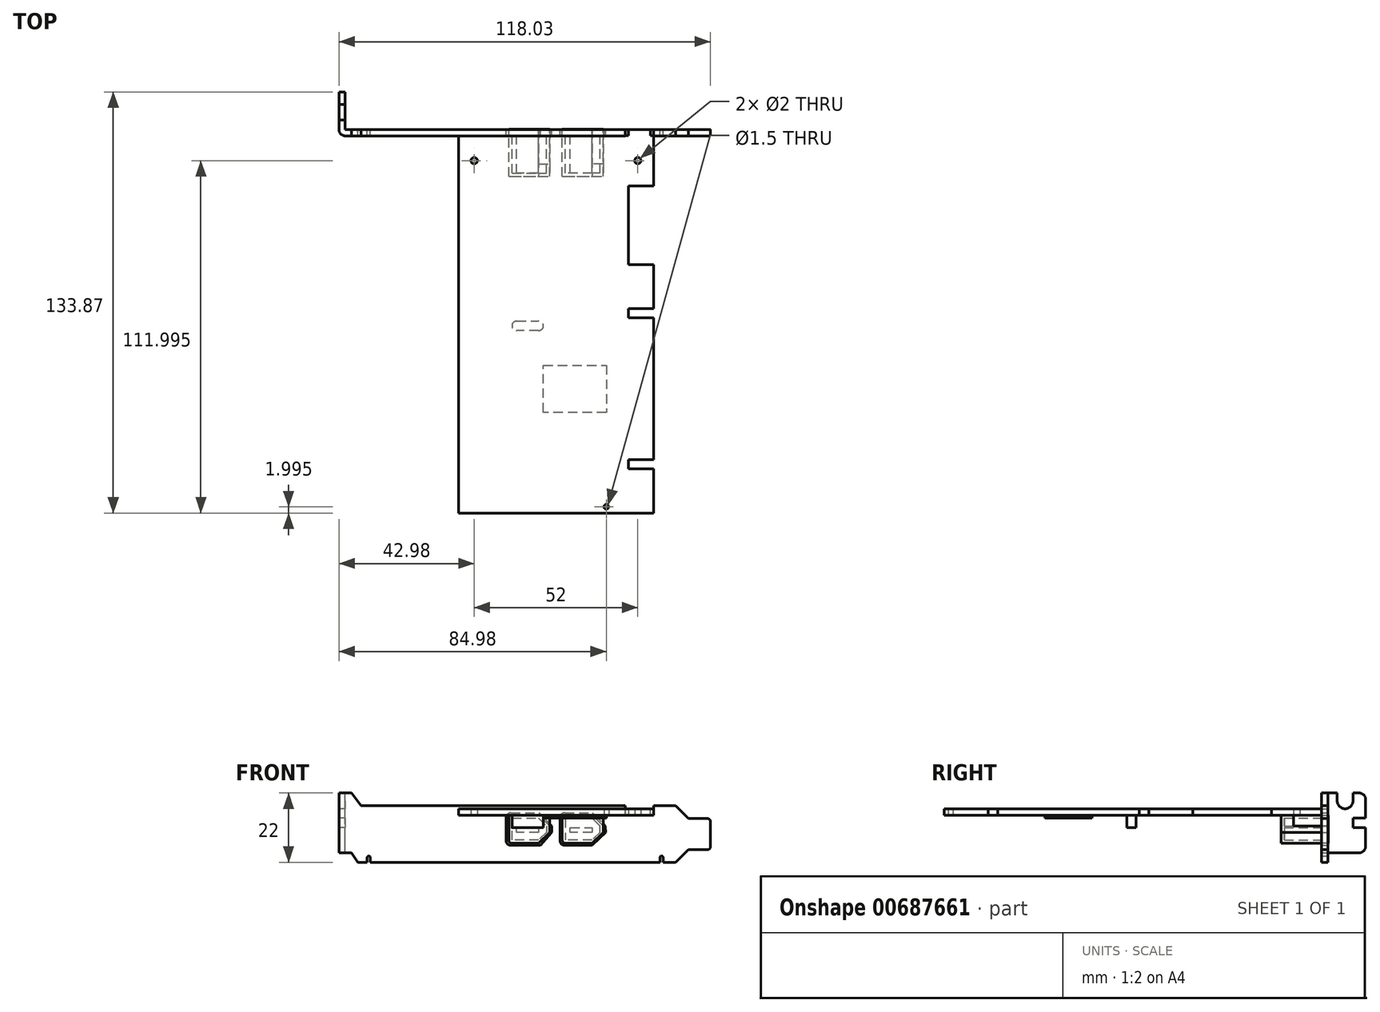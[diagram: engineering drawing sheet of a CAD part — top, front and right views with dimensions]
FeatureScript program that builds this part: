
annotation { "Feature Type Name" : "Feature", "Feature Type Description" : "" }
export const myFeature = defineFeature(function(context is Context, id is Id, definition is map)
    precondition{}
    {
        {
            var Q0;
            Q0=qCreatedBy(makeId("Top.planeOp"),FACE);
            var sketch = newSketch(context, id + "F0", { "sketchPlane" : qUnion([Q0])});
            skLineSegment(sketch, "E0", {"start": v(-31.18, 74.13) * mm, "end": v(-31.18, -45.87) * mm});
            skLineSegment(sketch, "E1", {"start": v(-31.18, -45.87) * mm, "end": v(30.82, -45.87) * mm});
            skLineSegment(sketch, "E2", {"start": v(30.82, -45.87) * mm, "end": v(30.82, -31.87) * mm});
            skLineSegment(sketch, "E3", {"start": v(30.82, -31.87) * mm, "end": v(22.82, -31.87) * mm});
            skLineSegment(sketch, "E4", {"start": v(22.82, -31.87) * mm, "end": v(22.82, -28.87) * mm});
            skLineSegment(sketch, "E5", {"start": v(22.82, -28.87) * mm, "end": v(30.82, -28.87) * mm});
            skLineSegment(sketch, "E6", {"start": v(30.82, -28.87) * mm, "end": v(30.82, 16.13) * mm});
            skLineSegment(sketch, "E7", {"start": v(30.82, 16.13) * mm, "end": v(22.82, 16.13) * mm});
            skLineSegment(sketch, "E8", {"start": v(22.82, 16.13) * mm, "end": v(22.82, 19.13) * mm});
            skLineSegment(sketch, "E9", {"start": v(22.82, 19.13) * mm, "end": v(30.82, 19.13) * mm});
            skLineSegment(sketch, "E10", {"start": v(30.82, 19.13) * mm, "end": v(30.82, 33.13) * mm});
            skLineSegment(sketch, "E11", {"start": v(30.82, 33.13) * mm, "end": v(22.82, 33.13) * mm});
            skLineSegment(sketch, "E12", {"start": v(22.82, 33.13) * mm, "end": v(22.82, 58.13) * mm});
            skLineSegment(sketch, "E13", {"start": v(22.82, 58.13) * mm, "end": v(30.82, 58.13) * mm});
            skLineSegment(sketch, "E14", {"start": v(30.82, 58.13) * mm, "end": v(30.82, 74.13) * mm});
            skLineSegment(sketch, "E15", {"start": v(30.82, 74.13) * mm, "end": v(-31.18, 74.13) * mm});
            skLineSegment(sketch, "E16", {"start": v(22.82, 74.13) * mm, "end": v(22.82, -45.87) * mm});
            skSolve(sketch);
        }
        {
            var Q0;
            Q0 = qSketchRegion(id + "F0", true);
            extrude(context, id + "F1", {"entities" : qUnion([Q0]), "depth" : 2 * mm, "offsetDistance" : 25 * mm});
        }
        {
            var Q0;
            Q0=makeQuery(id+"F1.opExtrude","CAP_FACE",FACE,{"disambiguationData":[OSD([sQuery(id+"F0.wireOp",EDGE,"E0"),sQuery(id+"F0.wireOp",EDGE,"E1"),sQuery(id+"F0.wireOp",EDGE,"E2"),sQuery(id+"F0.wireOp",EDGE,"E3"),sQuery(id+"F0.wireOp",EDGE,"E5"),sQuery(id+"F0.wireOp",EDGE,"E6"),sQuery(id+"F0.wireOp",EDGE,"E7"),sQuery(id+"F0.wireOp",EDGE,"E9"),sQuery(id+"F0.wireOp",EDGE,"E10"),sQuery(id+"F0.wireOp",EDGE,"E11"),sQuery(id+"F0.wireOp",EDGE,"E13"),sQuery(id+"F0.wireOp",EDGE,"E14"),sQuery(id+"F0.wireOp",EDGE,"E15"),sQuery(id+"F0.wireOp",EDGE,"E16")])],"isStart":false});
            var sketch = newSketch(context, id + "F2", { "sketchPlane" : qUnion([Q0])});
            skLineSegment(sketch, "E17", {"start": v(15.82, -17.22) * mm, "end": v(15.82, -13.87) * mm});
            skLineSegment(sketch, "E18", {"start": v(15.82, -13.87) * mm, "end": v(-4.18, -13.87) * mm});
            skLineSegment(sketch, "E19", {"start": v(-4.18, -13.87) * mm, "end": v(-4.18, 1.13) * mm});
            skLineSegment(sketch, "E20", {"start": v(-4.18, 1.13) * mm, "end": v(15.82, 1.13) * mm});
            skLineSegment(sketch, "E21", {"start": v(15.82, 1.13) * mm, "end": v(15.82, -13.87) * mm});
            skPoint(sketch, "E22.end.orphan", {"position": v(15.82, -17.22) * mm});
            skPoint(sketch, "E23.orphan", {"position": v(15.82, -45.87) * mm});
            skSolve(sketch);
        }
        {
            var Q0;
            Q0 = qSketchRegion(id + "F2", true);
            extrude(context, id + "F3", {"entities" : qUnion([Q0]), "operationType" : NewBodyOperationType.ADD, "oppositeDirection" : true, "depth" : 3 * mm, "offsetDistance" : 25 * mm});
        }
        {
            var Q0;
            Q0=makeQuery(id+"F1.opExtrude","CAP_FACE",FACE,{"disambiguationData":[OSD([sQuery(id+"F0.wireOp",EDGE,"E0"),sQuery(id+"F0.wireOp",EDGE,"E1"),sQuery(id+"F0.wireOp",EDGE,"E2"),sQuery(id+"F0.wireOp",EDGE,"E3"),sQuery(id+"F0.wireOp",EDGE,"E5"),sQuery(id+"F0.wireOp",EDGE,"E6"),sQuery(id+"F0.wireOp",EDGE,"E7"),sQuery(id+"F0.wireOp",EDGE,"E9"),sQuery(id+"F0.wireOp",EDGE,"E10"),sQuery(id+"F0.wireOp",EDGE,"E11"),sQuery(id+"F0.wireOp",EDGE,"E13"),sQuery(id+"F0.wireOp",EDGE,"E14"),sQuery(id+"F0.wireOp",EDGE,"E15"),sQuery(id+"F0.wireOp",EDGE,"E16")])],"isStart":true});
            var sketch = newSketch(context, id + "F4", { "sketchPlane" : qUnion([Q0])});
            skLineSegment(sketch, "E24", {"start": v(-5.68, -12.13) * mm, "end": v(-12.68, -12.13) * mm});
            skLineSegment(sketch, "E25", {"start": v(-14.18, -13.63) * mm, "end": v(-14.18, -13.63) * mm});
            skLineSegment(sketch, "E26", {"start": v(-12.68, -15.13) * mm, "end": v(-5.68, -15.13) * mm});
            skLineSegment(sketch, "E27", {"start": v(-5.68, -15.13) * mm, "end": v(-12.68, -15.13) * mm});
            skLineSegment(sketch, "E28", {"start": v(-4.18, -13.63) * mm, "end": v(-4.18, -13.63) * mm});
            skPoint(sketch, "E29.visualSharp", {"position": v(-14.18, -12.13) * mm});
            skArc(sketch, "E29.filletArc", {"start": v(-12.68, -12.13) * mm, "mid": v(-13.74, -12.56) * mm, "end": v(-14.18, -13.63) * mm});
            skPoint(sketch, "E30.visualSharp", {"position": v(-14.18, -15.13) * mm});
            skArc(sketch, "E30.filletArc", {"start": v(-14.18, -13.63) * mm, "mid": v(-13.74, -14.69) * mm, "end": v(-12.68, -15.13) * mm});
            skPoint(sketch, "E31.visualSharp", {"position": v(-4.18, -12.13) * mm});
            skArc(sketch, "E31.filletArc", {"start": v(-4.18, -13.63) * mm, "mid": v(-4.62, -12.56) * mm, "end": v(-5.68, -12.13) * mm});
            skPoint(sketch, "E32.visualSharp", {"position": v(-4.18, -15.13) * mm});
            skArc(sketch, "E32.filletArc", {"start": v(-5.68, -15.13) * mm, "mid": v(-4.62, -14.69) * mm, "end": v(-4.18, -13.63) * mm});
            skPoint(sketch, "E33.start.orphan", {"position": v(-14.18, -13.63) * mm});
            skSolve(sketch);
        }
        {
            var Q0;
            Q0 = qSketchRegion(id + "F4", true);
            extrude(context, id + "F5", {"entities" : qUnion([Q0]), "operationType" : NewBodyOperationType.ADD, "depth" : 4 * mm, "offsetDistance" : 25 * mm});
        }
        {
            var Q0;
            Q0=makeQuery(id+"F1.opExtrude","CAP_FACE",FACE,{"disambiguationData":[OSD([sQuery(id+"F0.wireOp",EDGE,"E0"),sQuery(id+"F0.wireOp",EDGE,"E1"),sQuery(id+"F0.wireOp",EDGE,"E2"),sQuery(id+"F0.wireOp",EDGE,"E3"),sQuery(id+"F0.wireOp",EDGE,"E5"),sQuery(id+"F0.wireOp",EDGE,"E6"),sQuery(id+"F0.wireOp",EDGE,"E7"),sQuery(id+"F0.wireOp",EDGE,"E9"),sQuery(id+"F0.wireOp",EDGE,"E10"),sQuery(id+"F0.wireOp",EDGE,"E11"),sQuery(id+"F0.wireOp",EDGE,"E13"),sQuery(id+"F0.wireOp",EDGE,"E14"),sQuery(id+"F0.wireOp",EDGE,"E15"),sQuery(id+"F0.wireOp",EDGE,"E16")])],"isStart":true});
            var sketch = newSketch(context, id + "F6", { "sketchPlane" : qUnion([Q0])});
            skLineSegment(sketch, "E34", {"start": v(22.82, 45.87) * mm, "end": v(22.82, -74.13) * mm});
            skPoint(sketch, "E35.end.orphan", {"position": v(15.82, 43.43) * mm});
            skCircle(sketch, "E36", {"center": v(15.82, 43.87) * mm, "radius": 0.75 * mm});
            skPoint(sketch, "E37.orphan", {"position": v(15.82, 45.87) * mm});
            skSolve(sketch);
        }
        {
            var Q0;
            Q0 = qSketchRegion(id + "F6", true);
            extrude(context, id + "F7", {"entities" : qUnion([Q0]), "operationType" : NewBodyOperationType.REMOVE, "oppositeDirection" : true, "depth" : 25 * mm, "offsetDistance" : 25 * mm});
        }
        {
            var Q0;
            Q0=makeQuery(id+"F1.opExtrude","CAP_FACE",FACE,{"disambiguationData":[OSD([sQuery(id+"F0.wireOp",EDGE,"E0"),sQuery(id+"F0.wireOp",EDGE,"E1"),sQuery(id+"F0.wireOp",EDGE,"E2"),sQuery(id+"F0.wireOp",EDGE,"E3"),sQuery(id+"F0.wireOp",EDGE,"E5"),sQuery(id+"F0.wireOp",EDGE,"E6"),sQuery(id+"F0.wireOp",EDGE,"E7"),sQuery(id+"F0.wireOp",EDGE,"E9"),sQuery(id+"F0.wireOp",EDGE,"E10"),sQuery(id+"F0.wireOp",EDGE,"E11"),sQuery(id+"F0.wireOp",EDGE,"E13"),sQuery(id+"F0.wireOp",EDGE,"E14"),sQuery(id+"F0.wireOp",EDGE,"E15"),sQuery(id+"F0.wireOp",EDGE,"E16")])],"isStart":true});
            var sketch = newSketch(context, id + "F8", { "sketchPlane" : qUnion([Q0])});
            skCircle(sketch, "E38", {"center": v(25.82, -66.13) * mm, "radius": 1 * mm});
            skPoint(sketch, "E39.orphan", {"position": v(30.82, -66.13) * mm});
            skCircle(sketch, "E40", {"center": v(-26.18, -66.13) * mm, "radius": 1 * mm});
            skPoint(sketch, "E41.orphan", {"position": v(-31.18, -66.13) * mm});
            skSolve(sketch);
        }
        {
            var Q0;
            Q0 = qSketchRegion(id + "F8", true);
            extrude(context, id + "F9", {"entities" : qUnion([Q0]), "operationType" : NewBodyOperationType.REMOVE, "oppositeDirection" : true, "depth" : 25 * mm, "offsetDistance" : 25 * mm});
        }
        {
            var Q0;
            Q0=makeQuery(id+"F1.opExtrude","CAP_FACE",FACE,{"disambiguationData":[OSD([sQuery(id+"F0.wireOp",EDGE,"E0"),sQuery(id+"F0.wireOp",EDGE,"E1"),sQuery(id+"F0.wireOp",EDGE,"E2"),sQuery(id+"F0.wireOp",EDGE,"E3"),sQuery(id+"F0.wireOp",EDGE,"E5"),sQuery(id+"F0.wireOp",EDGE,"E6"),sQuery(id+"F0.wireOp",EDGE,"E7"),sQuery(id+"F0.wireOp",EDGE,"E9"),sQuery(id+"F0.wireOp",EDGE,"E10"),sQuery(id+"F0.wireOp",EDGE,"E11"),sQuery(id+"F0.wireOp",EDGE,"E13"),sQuery(id+"F0.wireOp",EDGE,"E14"),sQuery(id+"F0.wireOp",EDGE,"E15"),sQuery(id+"F0.wireOp",EDGE,"E16")])],"isStart":true});
            var sketch = newSketch(context, id + "F10", { "sketchPlane" : qUnion([Q0])});
            skLineSegment(sketch, "E42", {"start": v(14.82, -74.13) * mm, "end": v(14.82, -61.13) * mm});
            skLineSegment(sketch, "E43", {"start": v(1.82, -61.13) * mm, "end": v(1.82, -74.13) * mm});
            skLineSegment(sketch, "E44", {"start": v(-15.18, -74.13) * mm, "end": v(-15.18, -61.13) * mm});
            skLineSegment(sketch, "E45", {"start": v(-2.18, -61.13) * mm, "end": v(-2.18, -74.13) * mm});
            skPoint(sketch, "E46.end.orphan", {"position": v(14.82, -67.43) * mm});
            skPoint(sketch, "E47.end.orphan", {"position": v(-15.18, -67.9) * mm});
            skPoint(sketch, "E47.start.orphan", {"position": v(-31.18, -67.43) * mm});
            skLineSegment(sketch, "E48", {"start": v(-15.18, -61.13) * mm, "end": v(-2.18, -61.13) * mm});
            skLineSegment(sketch, "E49", {"start": v(1.82, -61.13) * mm, "end": v(14.82, -61.13) * mm});
            skLineSegment(sketch, "E50", {"start": v(-15.18, -74.13) * mm, "end": v(-15.18, -76.13) * mm});
            skLineSegment(sketch, "E51", {"start": v(-2.18, -76.13) * mm, "end": v(-2.18, -74.13) * mm});
            skLineSegment(sketch, "E52", {"start": v(1.82, -74.13) * mm, "end": v(1.82, -76.13) * mm});
            skLineSegment(sketch, "E53", {"start": v(14.82, -76.13) * mm, "end": v(14.82, -74.13) * mm});
            skLineSegment(sketch, "E54", {"start": v(-15.18, -76.13) * mm, "end": v(-2.18, -76.13) * mm});
            skLineSegment(sketch, "E55", {"start": v(1.82, -76.13) * mm, "end": v(14.82, -76.13) * mm});
            skSolve(sketch);
        }
        {
            var Q0;
            Q0 = qSketchRegion(id + "F10", true);
            extrude(context, id + "F11", {"entities" : qUnion([Q0]), "operationType" : NewBodyOperationType.ADD, "depth" : 9 * mm, "offsetDistance" : 25 * mm});
        }
        {
            var Q0;
            Q0=makeQuery(id+"F11.opExtrude","CAP_EDGE",EDGE,{"disambiguationData":[OSD([sQuery(id+"F10.wireOp",EDGE,"E42"),sQuery(id+"F10.wireOp",EDGE,"E53")])],"isStart":false});
            chamfer(context, id + "F12", {"entities" : qUnion([Q0]), "width" : 3.5 * mm, "tangentPropagation" : true});
        }
        {
            var Q0;
            {var subQ0=sQuery(id+"F10.wireOp",EDGE,"E53");var subQ1=sQuery(id+"F10.wireOp",EDGE,"E42");Q0=makeQuery(id+"F11.boolean.opBoolean","SPLIT",EDGE,{"disambiguationData":[topologyDisambiguationEdgeConnected([makeQuery(id+"F11.opExtrude","CAP_FACE",FACE,{"disambiguationData":[OSD([subQ1,sQuery(id+"F10.wireOp",EDGE,"E43"),sQuery(id+"F10.wireOp",EDGE,"E49"),sQuery(id+"F10.wireOp",EDGE,"E52"),subQ0,sQuery(id+"F10.wireOp",EDGE,"E55")])],"isStart":true})])],"derivedFrom":makeQuery(id+"F11.opExtrude","CAP_EDGE",EDGE,{"disambiguationData":[OSD([subQ1,subQ0])],"isStart":true})});}
            chamfer(context, id + "F13", {"entities" : qUnion([Q0]), "width" : 3.5 * mm, "tangentPropagation" : true});
        }
        {
            var Q0;
            Q0=makeQuery(id+"F11.opExtrude","CAP_EDGE",EDGE,{"disambiguationData":[OSD([sQuery(id+"F10.wireOp",EDGE,"E43"),sQuery(id+"F10.wireOp",EDGE,"E52")])],"isStart":false});
            fillet(context, id + "F14", {"entities" : qUnion([Q0]), "radius" : 1 * mm, "tangentPropagation" : true, "allowEdgeOverflow" : false});
        }
        {
            var Q0;
            Q0=makeQuery(id+"F11.opExtrude","CAP_EDGE",EDGE,{"disambiguationData":[OSD([sQuery(id+"F10.wireOp",EDGE,"E44"),sQuery(id+"F10.wireOp",EDGE,"E50")])],"isStart":false});
            fillet(context, id + "F15", {"entities" : qUnion([Q0]), "radius" : 1 * mm, "tangentPropagation" : true, "allowEdgeOverflow" : false});
        }
        {
            var Q0;
            Q0=makeQuery(id+"F11.opExtrude","CAP_EDGE",EDGE,{"disambiguationData":[OSD([sQuery(id+"F10.wireOp",EDGE,"E45"),sQuery(id+"F10.wireOp",EDGE,"E51")])],"isStart":false});
            var Q1;
            {var subQ0=sQuery(id+"F10.wireOp",EDGE,"E51");var subQ1=sQuery(id+"F10.wireOp",EDGE,"E45");Q1=makeQuery(id+"F11.boolean.opBoolean","SPLIT",EDGE,{"disambiguationData":[topologyDisambiguationEdgeConnected([makeQuery(id+"F11.opExtrude","CAP_FACE",FACE,{"disambiguationData":[OSD([sQuery(id+"F10.wireOp",EDGE,"E44"),subQ1,sQuery(id+"F10.wireOp",EDGE,"E48"),sQuery(id+"F10.wireOp",EDGE,"E50"),subQ0,sQuery(id+"F10.wireOp",EDGE,"E54")])],"isStart":true})])],"derivedFrom":makeQuery(id+"F11.opExtrude","CAP_EDGE",EDGE,{"disambiguationData":[OSD([subQ1,subQ0])],"isStart":true})});}
            chamfer(context, id + "F16", {"entities" : qUnion([Q0, Q1]), "width" : 3.5 * mm, "tangentPropagation" : true});
        }
        {
            var Q0;
            Q0=makeQuery(id+"F11.opExtrude","SWEPT_FACE",FACE,{"disambiguationData":[OSD([sQuery(id+"F10.wireOp",EDGE,"E54")])]});
            var sketch = newSketch(context, id + "F17", { "sketchPlane" : qUnion([Q0])});
            skLineSegment(sketch, "E56", {"start": v(14.18, -1) * mm, "end": v(5.68, -1) * mm});
            skLineSegment(sketch, "E57", {"start": v(5.68, -1) * mm, "end": v(3.18, -3.5) * mm});
            skLineSegment(sketch, "E58", {"start": v(3.18, -3.5) * mm, "end": v(3.18, -5.5) * mm});
            skLineSegment(sketch, "E59", {"start": v(3.18, -5.5) * mm, "end": v(5.68, -8) * mm});
            skLineSegment(sketch, "E60", {"start": v(5.68, -8) * mm, "end": v(14.18, -8) * mm});
            skPoint(sketch, "E61.start.orphan", {"position": v(15.18, -4) * mm});
            skPoint(sketch, "E62.end.orphan", {"position": v(10.43, -1) * mm});
            skPoint(sketch, "E62.start.orphan", {"position": v(10.43, 0) * mm});
            skPoint(sketch, "E63.orphan", {"position": v(3.93, -1.75) * mm});
            skPoint(sketch, "E64.end.orphan", {"position": v(3.18, -4.5) * mm});
            skPoint(sketch, "E64.start.orphan", {"position": v(2.18, -4.5) * mm});
            skPoint(sketch, "E65.orphan", {"position": v(3.93, -7.25) * mm});
            skPoint(sketch, "E66.end.orphan", {"position": v(4.64, -6.54) * mm});
            skPoint(sketch, "E67.end.orphan", {"position": v(4.64, -2.46) * mm});
            skPoint(sketch, "E68.end.orphan", {"position": v(9.93, -8) * mm});
            skPoint(sketch, "E68.start.orphan", {"position": v(9.93, -9) * mm});
            skLineSegment(sketch, "E69", {"start": v(14.18, -8) * mm, "end": v(14.18, -1) * mm});
            skLineSegment(sketch, "E70", {"start": v(5.68, -5.5) * mm, "end": v(12.68, -5.5) * mm});
            skLineSegment(sketch, "E71", {"start": v(12.68, -5.5) * mm, "end": v(12.68, -4) * mm});
            skLineSegment(sketch, "E72", {"start": v(12.68, -4) * mm, "end": v(5.68, -4) * mm});
            skLineSegment(sketch, "E73", {"start": v(5.68, -4) * mm, "end": v(5.68, -5.5) * mm});
            skSolve(sketch);
        }
        {
            var Q0;
            Q0=makeQuery(id+"F17.imprint","IMPRINT",FACE,{"disambiguationData":[TD([[makeQuery(id+"F17.imprint","IMPRINT",EDGE,{"derivedFrom":sQuery(id+"F17.wireOp",EDGE,"E56")}),1.0]])]});
            extrude(context, id + "F18", {"entities" : qUnion([Q0]), "operationType" : NewBodyOperationType.REMOVE, "oppositeDirection" : true, "depth" : 14 * mm, "offsetDistance" : 25 * mm});
        }
        {
            var Q0;
            Q0=makeQuery(id+"F18.boolean.opBoolean","SPLIT",FACE,{"disambiguationData":[TD([makeQuery(id+"F18.opExtrude","SWEPT_FACE",FACE,{"disambiguationData":[OSD([sQuery(id+"F17.wireOp",EDGE,"E70")])]})])],"derivedFrom":makeQuery(id+"F11.opExtrude","SWEPT_FACE",FACE,{"disambiguationData":[OSD([sQuery(id+"F10.wireOp",EDGE,"E54")])]})});
            extrude(context, id + "F19", {"entities" : qUnion([Q0]), "operationType" : NewBodyOperationType.REMOVE, "oppositeDirection" : true, "depth" : 2 * mm, "offsetDistance" : 25 * mm});
        }
        {
            var Q0;
            Q0=makeQuery(id+"F11.opExtrude","SWEPT_FACE",FACE,{"disambiguationData":[OSD([sQuery(id+"F10.wireOp",EDGE,"E55")])]});
            var sketch = newSketch(context, id + "F20", { "sketchPlane" : qUnion([Q0])});
            skLineSegment(sketch, "E74", {"start": v(-2.82, -4) * mm, "end": v(-2.82, -8) * mm});
            skLineSegment(sketch, "E75", {"start": v(-2.82, -8) * mm, "end": v(-2.82, -1) * mm});
            skLineSegment(sketch, "E76", {"start": v(-2.82, -1) * mm, "end": v(-11.32, -1) * mm});
            skLineSegment(sketch, "E77", {"start": v(-13.82, -3.5) * mm, "end": v(-11.32, -1) * mm});
            skLineSegment(sketch, "E78", {"start": v(-13.82, -5.5) * mm, "end": v(-11.32, -8) * mm});
            skLineSegment(sketch, "E79", {"start": v(-11.32, -8) * mm, "end": v(-2.82, -8) * mm});
            skLineSegment(sketch, "E80", {"start": v(-13.82, -5.5) * mm, "end": v(-13.82, -3.5) * mm});
            skPoint(sketch, "E81.end.orphan", {"position": v(-7.07, -8) * mm});
            skPoint(sketch, "E81.start.orphan", {"position": v(-7.07, -9) * mm});
            skPoint(sketch, "E82.start.orphan", {"position": v(-1.82, -4) * mm});
            skPoint(sketch, "E83.end.orphan", {"position": v(-7.07, -1) * mm});
            skPoint(sketch, "E83.start.orphan", {"position": v(-7.07, 0) * mm});
            skLineSegment(sketch, "E84", {"start": v(-11.32, -5.5) * mm, "end": v(-4.32, -5.5) * mm});
            skLineSegment(sketch, "E85", {"start": v(-4.32, -5.5) * mm, "end": v(-4.32, -4) * mm});
            skLineSegment(sketch, "E86", {"start": v(-4.32, -4) * mm, "end": v(-11.32, -4) * mm});
            skLineSegment(sketch, "E87", {"start": v(-11.32, -4) * mm, "end": v(-11.32, -5.5) * mm});
            skSolve(sketch);
        }
        {
            var Q0;
            {var subQ3=sQuery(id+"F20.wireOp",EDGE,"E76");Q0=makeQuery(id+"F20.imprint","IMPRINT",FACE,{"disambiguationData":[TD([[makeQuery(id+"F20.imprint","IMPRINT",EDGE,{"derivedFrom":subQ3}),1.0]])]});}
            extrude(context, id + "F21", {"entities" : qUnion([Q0]), "operationType" : NewBodyOperationType.REMOVE, "oppositeDirection" : true, "depth" : 14 * mm, "offsetDistance" : 25 * mm});
        }
        {
            var Q0;
            Q0=makeQuery(id+"F21.boolean.opBoolean","SPLIT",FACE,{"disambiguationData":[TD([makeQuery(id+"F21.opExtrude","SWEPT_FACE",FACE,{"disambiguationData":[OSD([sQuery(id+"F20.wireOp",EDGE,"E84")])]})])],"derivedFrom":makeQuery(id+"F11.opExtrude","SWEPT_FACE",FACE,{"disambiguationData":[OSD([sQuery(id+"F10.wireOp",EDGE,"E55")])]})});
            extrude(context, id + "F22", {"entities" : qUnion([Q0]), "operationType" : NewBodyOperationType.REMOVE, "oppositeDirection" : true, "depth" : 2 * mm, "offsetDistance" : 25 * mm});
        }
        {
            var Q0;
            Q0=makeQuery(id+"F1.opExtrude","SWEPT_FACE",FACE,{"disambiguationData":[OSD([sQuery(id+"F0.wireOp",EDGE,"E15")])]});
            var sketch = newSketch(context, id + "F23", { "sketchPlane" : qUnion([Q0])});
            skLineSegment(sketch, "E88", {"start": v(-14.82, 0) * mm, "end": v(-11.32, 0) * mm});
            skLineSegment(sketch, "E89", {"start": v(-11.32, 0) * mm, "end": v(-14.82, -3.5) * mm});
            skLineSegment(sketch, "E90", {"start": v(-14.82, -3.5) * mm, "end": v(-14.82, 0) * mm});
            skLineSegment(sketch, "E91", {"start": v(2.18, 0) * mm, "end": v(2.18, -3.5) * mm});
            skLineSegment(sketch, "E92", {"start": v(2.18, -3.5) * mm, "end": v(5.68, 0) * mm});
            skLineSegment(sketch, "E93", {"start": v(5.68, 0) * mm, "end": v(2.18, 0) * mm});
            skSolve(sketch);
        }
        {
            var Q0;
            Q0=makeQuery(id+"F23.imprint","IMPRINT",FACE,{"disambiguationData":[TD([[makeQuery(id+"F23.imprint","IMPRINT",EDGE,{"derivedFrom":sQuery(id+"F23.wireOp",EDGE,"E88")}),-1.0]])]});
            extrude(context, id + "F24", {"entities" : qUnion([Q0]), "operationType" : NewBodyOperationType.REMOVE, "oppositeDirection" : true, "depth" : 9 * mm, "offsetDistance" : 25 * mm});
        }
        {
            var Q0;
            Q0=makeQuery(id+"F1.opExtrude","SWEPT_FACE",FACE,{"disambiguationData":[OSD([sQuery(id+"F0.wireOp",EDGE,"E15")])]});
            var sketch = newSketch(context, id + "F25", { "sketchPlane" : qUnion([Q0])});
            skLineSegment(sketch, "E94", {"start": v(5.68, 0) * mm, "end": v(2.18, 0) * mm});
            skLineSegment(sketch, "E95", {"start": v(2.18, 0) * mm, "end": v(2.18, -3.5) * mm});
            skLineSegment(sketch, "E96", {"start": v(2.18, -3.5) * mm, "end": v(5.68, 0) * mm});
            skSolve(sketch);
        }
        {
            var Q0;
            Q0=makeQuery(id+"F25.imprint","IMPRINT",FACE,{"disambiguationData":[TD([[makeQuery(id+"F25.imprint","IMPRINT",EDGE,{"derivedFrom":sQuery(id+"F25.wireOp",EDGE,"E94")}),1.0]])]});
            extrude(context, id + "F26", {"entities" : qUnion([Q0]), "operationType" : NewBodyOperationType.REMOVE, "oppositeDirection" : true, "depth" : 9 * mm, "offsetDistance" : 25 * mm});
        }
        {
            var Q0;
            Q0=qCreatedBy(makeId("Front.planeOp"),FACE);
            cPlane(context, id + "F27", {"entities" : qUnion([Q0]), "cplaneType" : CPlaneType.OFFSET, "offset" : 76 * mm, "oppositeDirection" : true, "width" : 150 * mm, "height" : 150 * mm});
        }
        {
            var Q0;
            Q0=qCreatedBy(id+"F27.planeOp",FACE);
            var sketch = newSketch(context, id + "F28", { "sketchPlane" : qUnion([Q0])});
            skLineSegment(sketch, "E97", {"start": v(1.84, 3) * mm, "end": v(21.84, 3) * mm});
            skLineSegment(sketch, "E98", {"start": v(21.84, 3) * mm, "end": v(21.84, 0.5) * mm});
            skLineSegment(sketch, "E99", {"start": v(22.34, 0) * mm, "end": v(22.34, 0) * mm});
            skLineSegment(sketch, "E100", {"start": v(22.84, 0.5) * mm, "end": v(22.84, 2) * mm});
            skLineSegment(sketch, "E101", {"start": v(22.84, 2) * mm, "end": v(29.84, 2) * mm});
            skLineSegment(sketch, "E102", {"start": v(29.84, 2) * mm, "end": v(29.84, 0.5) * mm});
            skLineSegment(sketch, "E103", {"start": v(30.34, 0) * mm, "end": v(30.34, 0) * mm});
            skLineSegment(sketch, "E104", {"start": v(30.84, 0.5) * mm, "end": v(30.84, 3) * mm});
            skLineSegment(sketch, "E105", {"start": v(30.84, 3) * mm, "end": v(37.84, 3) * mm});
            skLineSegment(sketch, "E106", {"start": v(48.87, -6.04) * mm, "end": v(48.87, -2.04) * mm});
            skLineSegment(sketch, "E107", {"start": v(37.84, -15) * mm, "end": v(33.84, -15) * mm});
            skLineSegment(sketch, "E108", {"start": v(33.84, -15) * mm, "end": v(33.84, -13.5) * mm});
            skLineSegment(sketch, "E109", {"start": v(33.34, -13) * mm, "end": v(33.34, -13) * mm});
            skLineSegment(sketch, "E110", {"start": v(32.84, -13.5) * mm, "end": v(32.84, -15) * mm});
            skLineSegment(sketch, "E111", {"start": v(32.84, -15) * mm, "end": v(-59.16, -15) * mm});
            skLineSegment(sketch, "E112", {"start": v(-59.16, -15) * mm, "end": v(-59.16, -13.5) * mm});
            skLineSegment(sketch, "E113", {"start": v(-59.66, -13) * mm, "end": v(-59.66, -13) * mm});
            skLineSegment(sketch, "E114", {"start": v(-60.16, -13.5) * mm, "end": v(-60.16, -15) * mm});
            skLineSegment(sketch, "E115", {"start": v(-60.16, -15) * mm, "end": v(-63.16, -15) * mm});
            skLineSegment(sketch, "E116", {"start": v(-63.16, -15) * mm, "end": v(-65.16, -12) * mm});
            skLineSegment(sketch, "E117", {"start": v(0, 3) * mm, "end": v(-62.16, 3) * mm});
            skLineSegment(sketch, "E118", {"start": v(-62.16, 3) * mm, "end": v(-65.16, 7) * mm});
            skPoint(sketch, "E119.start.orphan", {"position": v(-62.16, 4) * mm});
            skLineSegment(sketch, "E120", {"start": v(-9.45, 0) * mm, "end": v(-9.45, 0.7) * mm});
            skLineSegment(sketch, "E121", {"start": v(-15.34, -4.2) * mm, "end": v(-16.04, -4.2) * mm});
            skLineSegment(sketch, "E122", {"start": v(-9.92, -8.95) * mm, "end": v(-9.92, -9.65) * mm});
            skLineSegment(sketch, "E123", {"start": v(-9.92, -9.65) * mm, "end": v(-14.54, -9.65) * mm});
            skLineSegment(sketch, "E124", {"start": v(-16.04, -8.15) * mm, "end": v(-16.04, -4.2) * mm});
            skLineSegment(sketch, "E125", {"start": v(-16.04, -4.2) * mm, "end": v(-16.04, -0.8) * mm});
            skLineSegment(sketch, "E126", {"start": v(-14.54, 0.7) * mm, "end": v(-9.45, 0.7) * mm});
            skLineSegment(sketch, "E127", {"start": v(-5.6, 0) * mm, "end": v(-5.6, 0.7) * mm});
            skLineSegment(sketch, "E128", {"start": v(-5.6, 0.7) * mm, "end": v(-9.45, 0.7) * mm});
            skLineSegment(sketch, "E129", {"start": v(-2.2, -3.53) * mm, "end": v(-1.5, -3.53) * mm});
            skLineSegment(sketch, "E130", {"start": v(-1.5, -3.53) * mm, "end": v(-5.6, 0.7) * mm});
            skLineSegment(sketch, "E131", {"start": v(-2.2, -5.52) * mm, "end": v(-1.5, -5.52) * mm});
            skLineSegment(sketch, "E132", {"start": v(-1.5, -5.52) * mm, "end": v(-1.5, -3.53) * mm});
            skLineSegment(sketch, "E133", {"start": v(-5.6, -9.12) * mm, "end": v(-5.1, -9.62) * mm});
            skLineSegment(sketch, "E134", {"start": v(-5.1, -9.62) * mm, "end": v(-1.5, -5.52) * mm});
            skLineSegment(sketch, "E135", {"start": v(-9.92, -9.65) * mm, "end": v(-5.1, -9.62) * mm});
            skPoint(sketch, "E136.visualSharp", {"position": v(-16.04, -9.65) * mm});
            skArc(sketch, "E136.filletArc", {"start": v(-16.04, -8.15) * mm, "mid": v(-15.6, -9.2) * mm, "end": v(-14.54, -9.65) * mm});
            skPoint(sketch, "E137.visualSharp", {"position": v(-16.04, 0.7) * mm});
            skArc(sketch, "E137.filletArc", {"start": v(-14.54, 0.7) * mm, "mid": v(-15.6, 0.26) * mm, "end": v(-16.04, -0.8) * mm});
            skLineSegment(sketch, "E138", {"start": v(7.34, 0) * mm, "end": v(7.34, 0.7) * mm});
            skLineSegment(sketch, "E139", {"start": v(14.82, -3.47) * mm, "end": v(15.52, -3.47) * mm});
            skLineSegment(sketch, "E140", {"start": v(14.85, -5.53) * mm, "end": v(15.55, -5.53) * mm});
            skLineSegment(sketch, "E141", {"start": v(11.27, -9.14) * mm, "end": v(11.27, -9.62) * mm});
            skLineSegment(sketch, "E142", {"start": v(11.27, -9.62) * mm, "end": v(15.55, -5.53) * mm});
            skLineSegment(sketch, "E143", {"start": v(15.52, -3.47) * mm, "end": v(15.55, -5.53) * mm});
            skLineSegment(sketch, "E144", {"start": v(11.42, 0) * mm, "end": v(11.42, 0.7) * mm});
            skLineSegment(sketch, "E145", {"start": v(11.42, 0.7) * mm, "end": v(7.34, 0.7) * mm});
            skLineSegment(sketch, "E146", {"start": v(11.42, 0.7) * mm, "end": v(15.52, -3.47) * mm});
            skLineSegment(sketch, "E147", {"start": v(0, 3) * mm, "end": v(1.84, 3) * mm});
            skPoint(sketch, "E148.start.orphan", {"position": v(1.84, 0) * mm});
            skPoint(sketch, "E149.start.orphan", {"position": v(1.33, 0.7) * mm});
            skLineSegment(sketch, "E150", {"start": v(1.8, -4) * mm, "end": v(1.1, -4) * mm});
            skLineSegment(sketch, "E151", {"start": v(11.27, -9.62) * mm, "end": v(2.6, -9.62) * mm});
            skLineSegment(sketch, "E152", {"start": v(1.1, -8.12) * mm, "end": v(1.1, -4) * mm});
            skLineSegment(sketch, "E153", {"start": v(7.34, 0.7) * mm, "end": v(2.6, 0.7) * mm});
            skLineSegment(sketch, "E154", {"start": v(1.1, -0.8) * mm, "end": v(1.1, -4) * mm});
            skPoint(sketch, "E155.visualSharp", {"position": v(1.1, -9.62) * mm});
            skArc(sketch, "E155.filletArc", {"start": v(1.1, -8.12) * mm, "mid": v(1.53, -9.18) * mm, "end": v(2.6, -9.62) * mm});
            skPoint(sketch, "E156.visualSharp", {"position": v(1.1, 0.7) * mm});
            skArc(sketch, "E156.filletArc", {"start": v(2.6, 0.7) * mm, "mid": v(1.53, 0.26) * mm, "end": v(1.1, -0.8) * mm});
            skPoint(sketch, "E157.visualSharp", {"position": v(33.84, -13) * mm});
            skArc(sketch, "E157.filletArc", {"start": v(33.84, -13.5) * mm, "mid": v(33.7, -13.15) * mm, "end": v(33.34, -13) * mm});
            skPoint(sketch, "E158.visualSharp", {"position": v(32.84, -13) * mm});
            skArc(sketch, "E158.filletArc", {"start": v(33.34, -13) * mm, "mid": v(33, -13.15) * mm, "end": v(32.84, -13.5) * mm});
            skPoint(sketch, "E159.visualSharp", {"position": v(30.84, 0) * mm});
            skArc(sketch, "E159.filletArc", {"start": v(30.34, 0) * mm, "mid": v(30.7, 0.15) * mm, "end": v(30.84, 0.5) * mm});
            skPoint(sketch, "E160.visualSharp", {"position": v(29.84, 0) * mm});
            skArc(sketch, "E160.filletArc", {"start": v(29.84, 0.5) * mm, "mid": v(30, 0.15) * mm, "end": v(30.34, 0) * mm});
            skPoint(sketch, "E161.visualSharp", {"position": v(22.84, 0) * mm});
            skArc(sketch, "E161.filletArc", {"start": v(22.34, 0) * mm, "mid": v(22.7, 0.15) * mm, "end": v(22.84, 0.5) * mm});
            skPoint(sketch, "E162.visualSharp", {"position": v(21.84, 0) * mm});
            skArc(sketch, "E162.filletArc", {"start": v(21.84, 0.5) * mm, "mid": v(22, 0.15) * mm, "end": v(22.34, 0) * mm});
            skPoint(sketch, "E163.visualSharp", {"position": v(-59.16, -13) * mm});
            skArc(sketch, "E163.filletArc", {"start": v(-59.16, -13.5) * mm, "mid": v(-59.3, -13.15) * mm, "end": v(-59.66, -13) * mm});
            skPoint(sketch, "E164.visualSharp", {"position": v(-60.16, -13) * mm});
            skArc(sketch, "E164.filletArc", {"start": v(-59.66, -13) * mm, "mid": v(-60, -13.15) * mm, "end": v(-60.16, -13.5) * mm});
            skPoint(sketch, "E165.start.orphan", {"position": v(37.84, -6) * mm});
            skLineSegment(sketch, "E166", {"start": v(48.87, -6.04) * mm, "end": v(48.87, -10.04) * mm});
            skLineSegment(sketch, "E167", {"start": v(47.87, -11.04) * mm, "end": v(41.87, -11.04) * mm});
            skLineSegment(sketch, "E168", {"start": v(41.87, -11.04) * mm, "end": v(37.84, -15) * mm});
            skLineSegment(sketch, "E169", {"start": v(47.87, -1.04) * mm, "end": v(41.87, -1.04) * mm});
            skLineSegment(sketch, "E170", {"start": v(41.87, -1.04) * mm, "end": v(37.84, 3) * mm});
            skPoint(sketch, "E171.visualSharp", {"position": v(48.87, -11.04) * mm});
            skArc(sketch, "E171.filletArc", {"start": v(47.87, -11.04) * mm, "mid": v(48.57, -10.75) * mm, "end": v(48.87, -10.04) * mm});
            skPoint(sketch, "E172.visualSharp", {"position": v(48.87, -1.04) * mm});
            skArc(sketch, "E172.filletArc", {"start": v(48.87, -2.04) * mm, "mid": v(48.57, -1.34) * mm, "end": v(47.87, -1.04) * mm});
            skLineSegment(sketch, "E173", {"start": v(-65.16, 7) * mm, "end": v(-71.16, 7) * mm});
            skLineSegment(sketch, "E174", {"start": v(-65.16, -12) * mm, "end": v(-71.16, -12) * mm});
            skLineSegment(sketch, "E175", {"start": v(-71.16, -12) * mm, "end": v(-71.16, 7) * mm});
            skLineSegment(sketch, "E176", {"start": v(-69.16, -4.9) * mm, "end": v(-69.16, -12) * mm});
            skLineSegment(sketch, "E177", {"start": v(-69.16, -12) * mm, "end": v(-69.16, 7) * mm});
            skSolve(sketch);
        }
        {
            var Q0;
            Q0=makeQuery(id+"F28.imprint","IMPRINT",FACE,{"disambiguationData":[TD([[makeQuery(id+"F28.imprint","IMPRINT",EDGE,{"derivedFrom":sQuery(id+"F28.wireOp",EDGE,"E97")}),-1.0]])]});
            extrude(context, id + "F29", {"entities" : qUnion([Q0]), "operationType" : NewBodyOperationType.ADD, "depth" : 2 * mm, "offsetDistance" : 25 * mm});
        }
        {
            var Q0;
            Q0=makeQuery(id+"F29.opExtrude","CAP_FACE",FACE,{"disambiguationData":[OSD([sQuery(id+"F28.wireOp",EDGE,"E97"),sQuery(id+"F28.wireOp",EDGE,"E98"),sQuery(id+"F28.wireOp",EDGE,"E100"),sQuery(id+"F28.wireOp",EDGE,"E101"),sQuery(id+"F28.wireOp",EDGE,"E102"),sQuery(id+"F28.wireOp",EDGE,"E104"),sQuery(id+"F28.wireOp",EDGE,"E105"),sQuery(id+"F28.wireOp",EDGE,"E106"),sQuery(id+"F28.wireOp",EDGE,"E107"),sQuery(id+"F28.wireOp",EDGE,"E108"),sQuery(id+"F28.wireOp",EDGE,"E110"),sQuery(id+"F28.wireOp",EDGE,"E111"),sQuery(id+"F28.wireOp",EDGE,"E112"),sQuery(id+"F28.wireOp",EDGE,"E114"),sQuery(id+"F28.wireOp",EDGE,"E115"),sQuery(id+"F28.wireOp",EDGE,"E116"),sQuery(id+"F28.wireOp",EDGE,"E117"),sQuery(id+"F28.wireOp",EDGE,"E118"),sQuery(id+"F28.wireOp",EDGE,"E123"),sQuery(id+"F28.wireOp",EDGE,"E124"),sQuery(id+"F28.wireOp",EDGE,"E125"),sQuery(id+"F28.wireOp",EDGE,"E126"),sQuery(id+"F28.wireOp",EDGE,"E128"),sQuery(id+"F28.wireOp",EDGE,"E130"),sQuery(id+"F28.wireOp",EDGE,"E132"),sQuery(id+"F28.wireOp",EDGE,"E134"),sQuery(id+"F28.wireOp",EDGE,"E135"),sQuery(id+"F28.wireOp",EDGE,"E136.filletArc"),sQuery(id+"F28.wireOp",EDGE,"E137.filletArc"),sQuery(id+"F28.wireOp",EDGE,"E142"),sQuery(id+"F28.wireOp",EDGE,"E143"),sQuery(id+"F28.wireOp",EDGE,"E145"),sQuery(id+"F28.wireOp",EDGE,"E146"),sQuery(id+"F28.wireOp",EDGE,"E147"),sQuery(id+"F28.wireOp",EDGE,"E151"),sQuery(id+"F28.wireOp",EDGE,"E152"),sQuery(id+"F28.wireOp",EDGE,"E153"),sQuery(id+"F28.wireOp",EDGE,"E154"),sQuery(id+"F28.wireOp",EDGE,"E155.filletArc"),sQuery(id+"F28.wireOp",EDGE,"E156.filletArc"),sQuery(id+"F28.wireOp",EDGE,"E157.filletArc"),sQuery(id+"F28.wireOp",EDGE,"E158.filletArc"),sQuery(id+"F28.wireOp",EDGE,"E159.filletArc"),sQuery(id+"F28.wireOp",EDGE,"E160.filletArc"),sQuery(id+"F28.wireOp",EDGE,"E161.filletArc"),sQuery(id+"F28.wireOp",EDGE,"E162.filletArc"),sQuery(id+"F28.wireOp",EDGE,"E163.filletArc"),sQuery(id+"F28.wireOp",EDGE,"E164.filletArc"),sQuery(id+"F28.wireOp",EDGE,"E166"),sQuery(id+"F28.wireOp",EDGE,"E167"),sQuery(id+"F28.wireOp",EDGE,"E168"),sQuery(id+"F28.wireOp",EDGE,"E169"),sQuery(id+"F28.wireOp",EDGE,"E170"),sQuery(id+"F28.wireOp",EDGE,"E171.filletArc"),sQuery(id+"F28.wireOp",EDGE,"E172.filletArc"),sQuery(id+"F28.wireOp",EDGE,"E173"),sQuery(id+"F28.wireOp",EDGE,"E174"),sQuery(id+"F28.wireOp",EDGE,"E177")])],"isStart":true});
            var sketch = newSketch(context, id + "F30", { "sketchPlane" : qUnion([Q0])});
            skLineSegment(sketch, "E178", {"start": v(67.16, -5.67) * mm, "end": v(67.16, -12) * mm});
            skLineSegment(sketch, "E179", {"start": v(67.16, -12) * mm, "end": v(67.16, 7) * mm});
            skSolve(sketch);
        }
        {
            var Q0;
            {var subQ0=makeQuery(id+"F29.opExtrude","CAP_EDGE",EDGE,{"disambiguationData":[OSD([sQuery(id+"F28.wireOp",EDGE,"E177")])],"isStart":true});Q0=makeQuery(id+"F30.imprint","IMPRINT",FACE,{"disambiguationData":[TD([[makeQuery(id+"F30.imprint","IMPRINT",EDGE,{"derivedFrom":subQ0}),1.0]])]});}
            extrude(context, id + "F31", {"entities" : qUnion([Q0]), "operationType" : NewBodyOperationType.ADD, "depth" : 12 * mm, "offsetDistance" : 25 * mm});
        }
        {
            var Q0;
            Q0=makeQuery(id+"F31.opExtrude","CAP_EDGE",EDGE,{"disambiguationData":[OSD([sQuery(id+"F28.wireOp",EDGE,"E174")])],"isStart":false});
            var Q1;
            Q1=makeQuery(id+"F31.opExtrude","CAP_EDGE",EDGE,{"disambiguationData":[OSD([sQuery(id+"F28.wireOp",EDGE,"E173")])],"isStart":false});
            fillet(context, id + "F32", {"entities" : qUnion([Q0, Q1]), "radius" : 2 * mm, "tangentPropagation" : true, "allowEdgeOverflow" : false});
        }
        {
            var Q0;
            Q0=makeQuery(id+"F29.opExtrude","CAP_EDGE",EDGE,{"disambiguationData":[OSD([sQuery(id+"F28.wireOp",EDGE,"E177")])],"isStart":false});
            fillet(context, id + "F33", {"entities" : qUnion([Q0]), "radius" : 2 * mm, "tangentPropagation" : true, "allowEdgeOverflow" : false});
        }
        {
            var Q0;
            {var subQ0=sQuery(id+"F28.wireOp",EDGE,"E177");Q0=makeQuery(id+"F31.boolean.opBoolean","MERGE",FACE,{"derivedFrom":[makeQuery(id+"F29.opExtrude","SWEPT_FACE",FACE,{"disambiguationData":[OSD([subQ0])]}),makeQuery(id+"F31.opExtrude","SWEPT_FACE",FACE,{"disambiguationData":[OSD([subQ0])]})]});}
            var sketch = newSketch(context, id + "F34", { "sketchPlane" : qUnion([Q0])});
            skLineSegment(sketch, "E180", {"start": v(-88, -4) * mm, "end": v(-84, -4) * mm});
            skLineSegment(sketch, "E181", {"start": v(-84, -1) * mm, "end": v(-88, -1) * mm});
            skLineSegment(sketch, "E182", {"start": v(-88, -1) * mm, "end": v(-88, -4) * mm});
            skPoint(sketch, "E183.end.orphan", {"position": v(-85.42, -4) * mm});
            skLineSegment(sketch, "E184", {"start": v(-84, -4) * mm, "end": v(-84, -1) * mm});
            skLineSegment(sketch, "E185", {"start": v(-88, -4) * mm, "end": v(-88, -1) * mm});
            skSolve(sketch);
        }
        {
            var Q0;
            Q0 = qSketchRegion(id + "F34", true);
            extrude(context, id + "F35", {"entities" : qUnion([Q0]), "operationType" : NewBodyOperationType.REMOVE, "oppositeDirection" : true, "depth" : 25 * mm, "offsetDistance" : 25 * mm});
        }
        {
            var Q0;
            {var subQ0=sQuery(id+"F28.wireOp",EDGE,"E177");Q0=makeQuery(id+"F31.boolean.opBoolean","MERGE",FACE,{"derivedFrom":[makeQuery(id+"F29.opExtrude","SWEPT_FACE",FACE,{"disambiguationData":[OSD([subQ0])]}),makeQuery(id+"F31.opExtrude","SWEPT_FACE",FACE,{"disambiguationData":[OSD([subQ0])]})]});}
            var sketch = newSketch(context, id + "F36", { "sketchPlane" : qUnion([Q0])});
            skLineSegment(sketch, "E186", {"start": v(-84, 7) * mm, "end": v(-84, 4.5) * mm});
            skLineSegment(sketch, "E187", {"start": v(-81.5, 2) * mm, "end": v(-81.5, 2) * mm});
            skLineSegment(sketch, "E188", {"start": v(-79, 4.5) * mm, "end": v(-79, 7) * mm});
            skPoint(sketch, "E189.visualSharp", {"position": v(-79, 2) * mm});
            skArc(sketch, "E189.filletArc", {"start": v(-81.5, 2) * mm, "mid": v(-79.73, 2.73) * mm, "end": v(-79, 4.5) * mm});
            skPoint(sketch, "E190.visualSharp", {"position": v(-84, 2) * mm});
            skArc(sketch, "E190.filletArc", {"start": v(-84, 4.5) * mm, "mid": v(-83.27, 2.73) * mm, "end": v(-81.5, 2) * mm});
            skPoint(sketch, "E191.end.orphan", {"position": v(-84, 4.36) * mm});
            skLineSegment(sketch, "E192", {"start": v(-79, 7) * mm, "end": v(-84, 7) * mm});
            skSolve(sketch);
        }
        {
            var Q0;
            Q0 = qSketchRegion(id + "F36", true);
            extrude(context, id + "F37", {"entities" : qUnion([Q0]), "operationType" : NewBodyOperationType.REMOVE, "oppositeDirection" : true, "depth" : 25 * mm, "offsetDistance" : 25 * mm});
        }
    });
